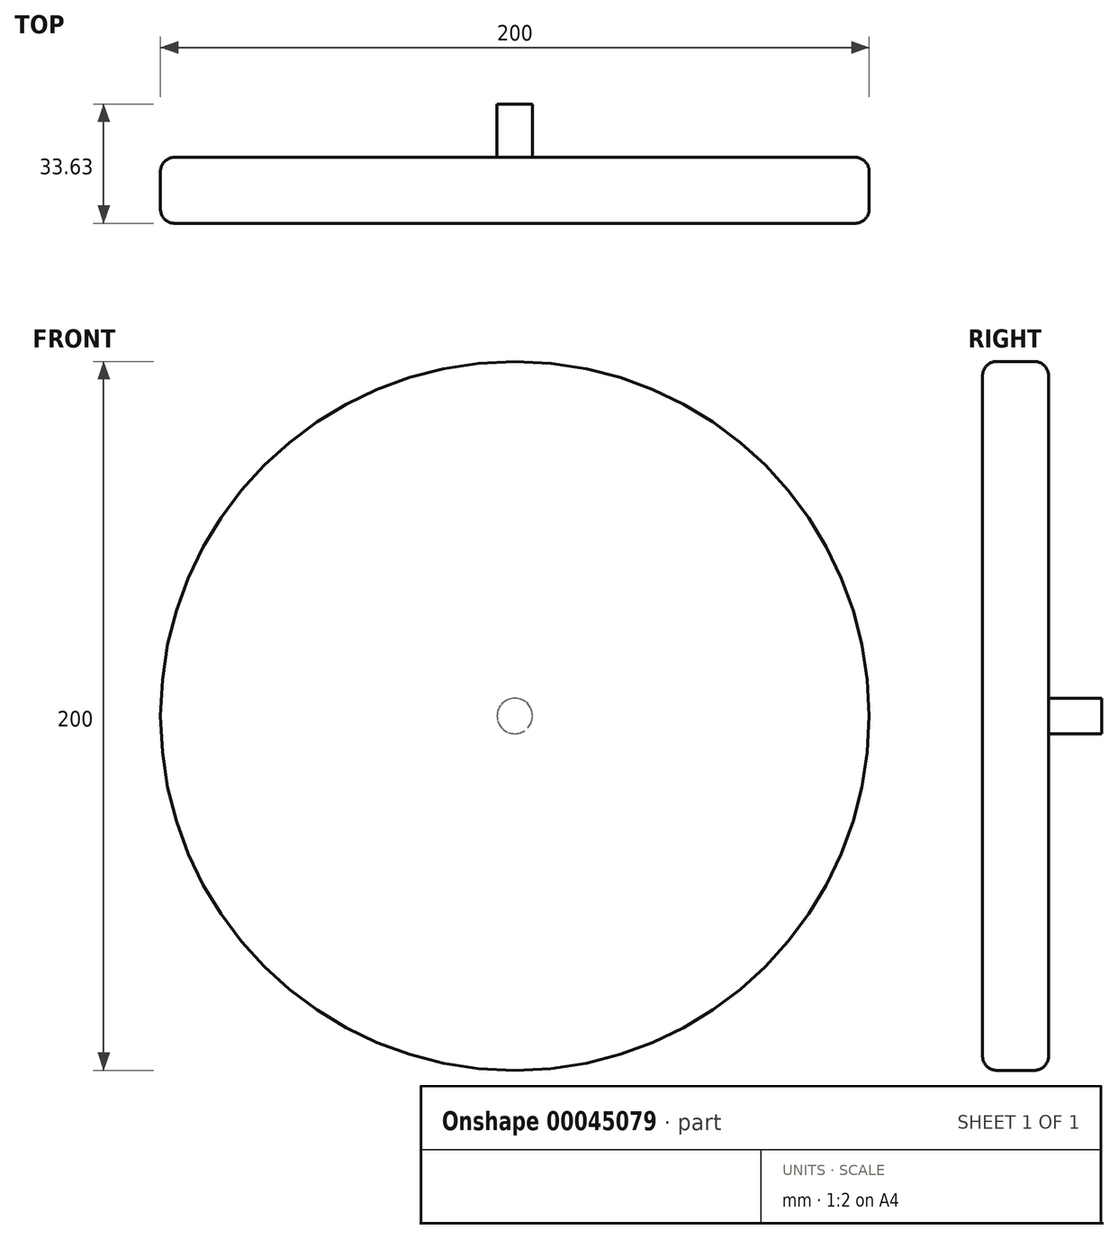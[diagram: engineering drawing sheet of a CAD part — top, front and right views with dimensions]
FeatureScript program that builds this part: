
annotation { "Feature Type Name" : "Feature", "Feature Type Description" : "" }
export const myFeature = defineFeature(function(context is Context, id is Id, definition is map)
    precondition{}
    {
        {
            var Q0;
            Q0=qCreatedBy(makeId("Front.planeOp"),FACE);
            var sketch = newSketch(context, id + "F0", { "sketchPlane" : qUnion([Q0])});
            skCircle(sketch, "E0", {"center": v(-44.57, 36.7) * mm, "radius": 100 * mm});
            skSolve(sketch);
        }
        {
            var Q0;
            Q0=makeQuery(id+"F0.imprint","IMPRINT",FACE,{"disambiguationData":[TD([[makeQuery(id+"F0.imprint","IMPRINT",EDGE,{"derivedFrom":sQuery(id+"F0.wireOp",EDGE,"E0")}),1.0]])]});
            extrude(context, id + "F1", {"entities" : qUnion([Q0]), "depth" : 18.63 * mm});
        }
        {
            var Q0;
            Q0=makeQuery(id+"F1.opExtrude","CAP_EDGE",EDGE,{"disambiguationData":[OSD([sQuery(id+"F0.wireOp",EDGE,"E0")])],"isStart":false});
            var Q1;
            Q1=makeQuery(id+"F1.opExtrude","CAP_EDGE",EDGE,{"disambiguationData":[OSD([sQuery(id+"F0.wireOp",EDGE,"E0")])],"isStart":true});
            fillet(context, id + "F2", {"entities" : qUnion([Q0, Q1]), "radius" : 4 * mm, "tangentPropagation" : true, "allowEdgeOverflow" : false});
        }
        {
            var Q0;
            Q0=makeQuery(id+"F1.opExtrude","CAP_FACE",FACE,{"disambiguationData":[OSD([sQuery(id+"F0.wireOp",EDGE,"E0")])],"isStart":true});
            var sketch = newSketch(context, id + "F3", { "sketchPlane" : qUnion([Q0])});
            skCircle(sketch, "E1", {"center": v(44.57, 36.7) * mm, "radius": 5 * mm});
            skSolve(sketch);
        }
        {
            var Q0;
            Q0=makeQuery(id+"F3.imprint","IMPRINT",FACE,{"disambiguationData":[TD([[makeQuery(id+"F3.imprint","IMPRINT",EDGE,{"derivedFrom":sQuery(id+"F3.wireOp",EDGE,"E1")}),1.0]])]});
            extrude(context, id + "F4", {"entities" : qUnion([Q0]), "operationType" : NewBodyOperationType.ADD, "depth" : 15 * mm});
        }
    });
